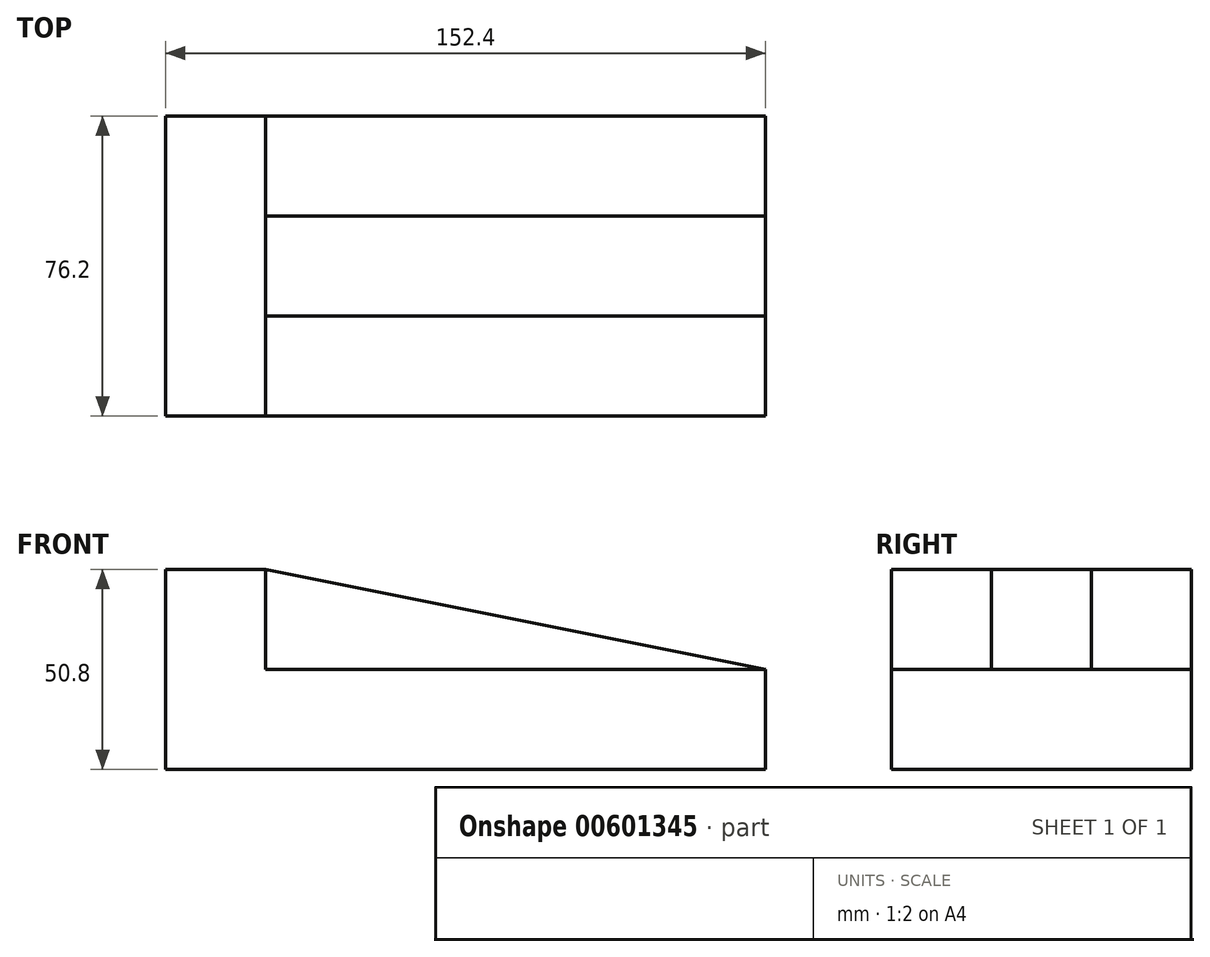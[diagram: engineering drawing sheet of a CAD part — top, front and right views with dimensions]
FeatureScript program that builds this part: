
annotation { "Feature Type Name" : "Feature", "Feature Type Description" : "" }
export const myFeature = defineFeature(function(context is Context, id is Id, definition is map)
    precondition{}
    {
        {
            var Q0;
            Q0=qCreatedBy(makeId("Front.planeOp"),FACE);
            var sketch = newSketch(context, id + "F0", { "sketchPlane" : qUnion([Q0])});
            skLineSegment(sketch, "E0", {"start": v(-77.41, 20.37) * mm, "end": v(-77.41, -30.43) * mm});
            skLineSegment(sketch, "E1", {"start": v(-77.41, -30.43) * mm, "end": v(74.99, -30.43) * mm});
            skLineSegment(sketch, "E2", {"start": v(74.99, -30.43) * mm, "end": v(74.99, -5.03) * mm});
            skLineSegment(sketch, "E3", {"start": v(74.99, -5.03) * mm, "end": v(-52.01, -5.03) * mm});
            skLineSegment(sketch, "E4", {"start": v(-52.01, -5.03) * mm, "end": v(-52.01, 20.37) * mm});
            skLineSegment(sketch, "E5", {"start": v(-52.01, 20.37) * mm, "end": v(-77.41, 20.37) * mm});
            skLineSegment(sketch, "E6", {"start": v(-52.01, 20.37) * mm, "end": v(74.99, -5.03) * mm});
            skSolve(sketch);
        }
        {
            var Q0;
            Q0=makeQuery(id+"F0.imprint","IMPRINT",FACE,{"disambiguationData":[TD([[makeQuery(id+"F0.imprint","IMPRINT",EDGE,{"derivedFrom":sQuery(id+"F0.wireOp",EDGE,"E0")}),1.0]])]});
            extrude(context, id + "F1", {"entities" : qUnion([Q0]), "depth" : 76.2 * mm, "offsetDistance" : 25.4 * mm});
        }
        {
            var Q0;
            Q0 = qSketchRegion(id + "F0", true);
            extrude(context, id + "F2", {"entities" : qUnion([Q0]), "operationType" : NewBodyOperationType.ADD, "depth" : 50.8 * mm, "offsetDistance" : 25.4 * mm});
        }
        {
            var Q0;
            {var subQ0=sQuery(id+"F0.wireOp",EDGE,"E5");var subQ1=sQuery(id+"F0.wireOp",EDGE,"E2");var subQ2=sQuery(id+"F0.wireOp",EDGE,"E1");var subQ3=sQuery(id+"F0.wireOp",EDGE,"E0");Q0=makeQuery(id+"F2.boolean.opBoolean","MERGE",FACE,{"derivedFrom":[makeQuery(id+"F1.opExtrude","CAP_FACE",FACE,{"disambiguationData":[OSD([subQ3,subQ2,subQ1,sQuery(id+"F0.wireOp",EDGE,"E3"),sQuery(id+"F0.wireOp",EDGE,"E4"),subQ0])],"isStart":true}),makeQuery(id+"F2.opExtrude","CAP_FACE",FACE,{"disambiguationData":[OSD([subQ3,subQ2,subQ1,subQ0,sQuery(id+"F0.wireOp",EDGE,"E6")])],"isStart":true})]});}
            var sketch = newSketch(context, id + "F3", { "sketchPlane" : qUnion([Q0])});
            skLineSegment(sketch, "E7", {"start": v(-74.99, -5.03) * mm, "end": v(52.01, -5.03) * mm});
            skLineSegment(sketch, "E8", {"start": v(52.01, -5.03) * mm, "end": v(52.01, 20.37) * mm});
            skSolve(sketch);
        }
        {
            var Q0;
            Q0=makeQuery(id+"F3.imprint","IMPRINT",FACE,{"disambiguationData":[TD([[makeQuery(id+"F3.imprint","IMPRINT",EDGE,{"derivedFrom":sQuery(id+"F3.wireOp",EDGE,"E7")}),1.0]])]});
            extrude(context, id + "F4", {"entities" : qUnion([Q0]), "operationType" : NewBodyOperationType.REMOVE, "oppositeDirection" : true, "depth" : 25.4 * mm, "offsetDistance" : 25.4 * mm});
        }
    });
